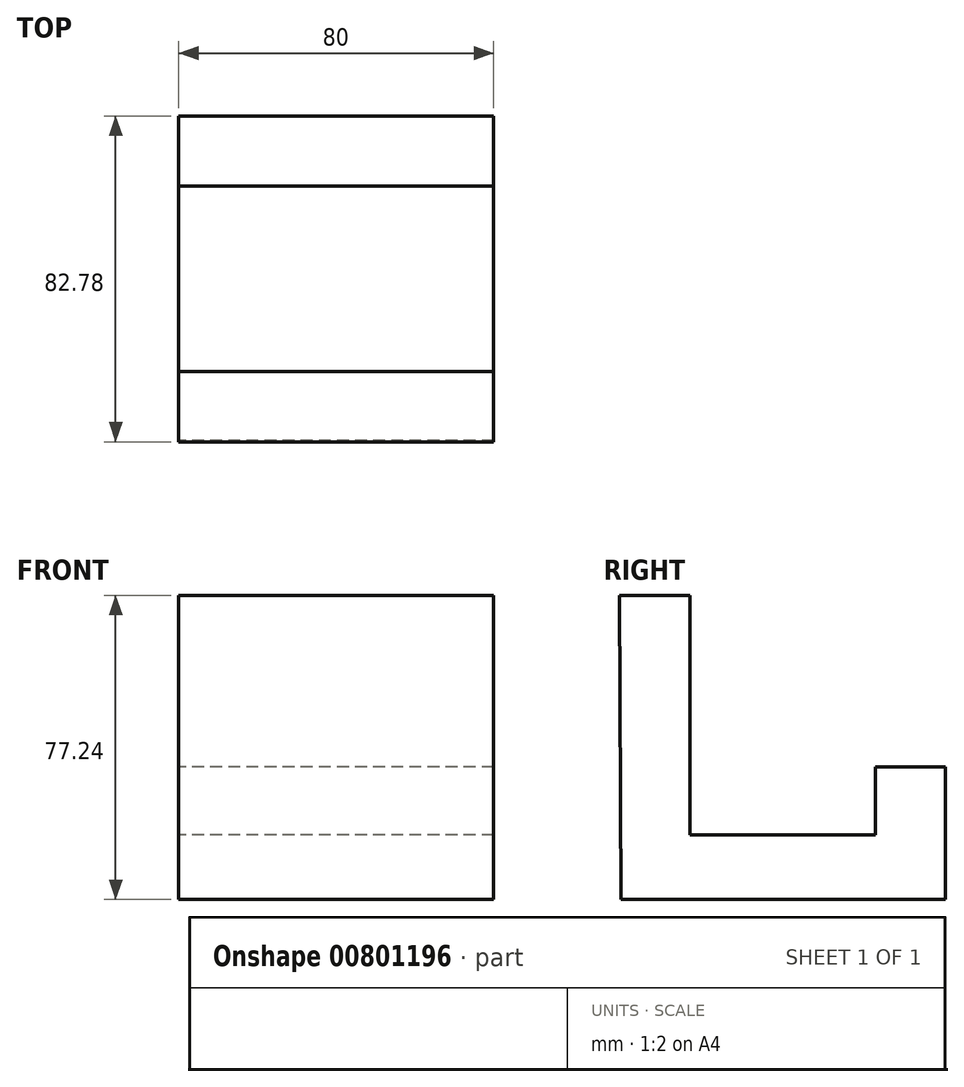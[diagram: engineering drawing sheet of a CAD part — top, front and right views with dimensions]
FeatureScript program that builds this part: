
annotation { "Feature Type Name" : "Feature", "Feature Type Description" : "" }
export const myFeature = defineFeature(function(context is Context, id is Id, definition is map)
    precondition{}
    {
        {
            var Q0;
            Q0=qCreatedBy(makeId("Right.planeOp"),FACE);
            var sketch = newSketch(context, id + "F0", { "sketchPlane" : qUnion([Q0])});
            skLineSegment(sketch, "E0", {"start": v(-37.63, -16.44) * mm, "end": v(44.76, -16.44) * mm});
            skLineSegment(sketch, "E1", {"start": v(44.76, 17.23) * mm, "end": v(26.93, 17.23) * mm});
            skLineSegment(sketch, "E2", {"start": v(26.93, 17.23) * mm, "end": v(26.93, 0) * mm});
            skLineSegment(sketch, "E3", {"start": v(26.93, 0) * mm, "end": v(-20.2, 0) * mm});
            skLineSegment(sketch, "E4", {"start": v(-20.2, 0) * mm, "end": v(-20.2, 60.8) * mm});
            skLineSegment(sketch, "E5", {"start": v(-20.2, 60.8) * mm, "end": v(-38.02, 60.8) * mm});
            skLineSegment(sketch, "E6", {"start": v(-38.02, 60.8) * mm, "end": v(-37.63, -16.44) * mm});
            skLineSegment(sketch, "E7", {"start": v(44.76, -16.44) * mm, "end": v(44.76, 17.23) * mm});
            skSolve(sketch);
        }
        {
            var Q0;
            Q0 = qSketchRegion(id + "F0", true);
            extrude(context, id + "F1", {"entities" : qUnion([Q0]), "depth" : 80 * mm, "offsetDistance" : 25.4 * mm});
        }
    });
